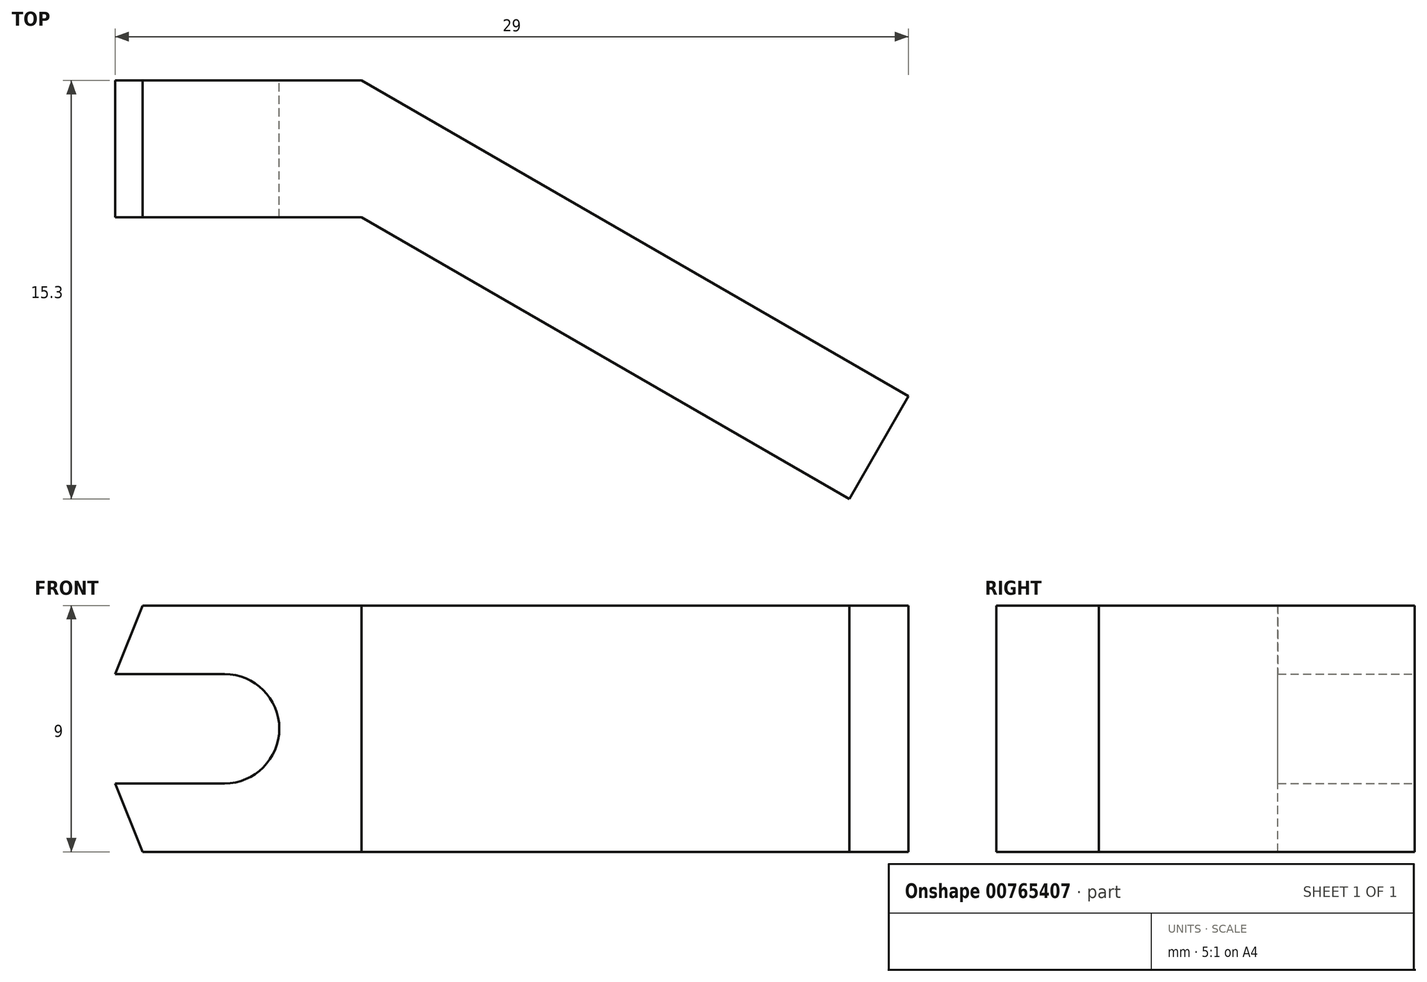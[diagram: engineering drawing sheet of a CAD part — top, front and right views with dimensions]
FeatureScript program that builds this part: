
annotation { "Feature Type Name" : "Feature", "Feature Type Description" : "" }
export const myFeature = defineFeature(function(context is Context, id is Id, definition is map)
    precondition{}
    {
        {
            var Q0;
            Q0=qCreatedBy(makeId("Front.planeOp"),FACE);
            var sketch = newSketch(context, id + "F0", { "sketchPlane" : qUnion([Q0])});
            skArc(sketch, "E0", {"start": v(0, -2) * mm, "mid": v(2, 0) * mm, "end": v(0, 2) * mm});
            skLineSegment(sketch, "E1", {"start": v(0, 2) * mm, "end": v(-4, 2) * mm});
            skLineSegment(sketch, "E2", {"start": v(0, -2) * mm, "end": v(-4, -2) * mm});
            skLineSegment(sketch, "E3", {"start": v(-3, -4.5) * mm, "end": v(-4, -2) * mm});
            skLineSegment(sketch, "E4", {"start": v(-3, 4.5) * mm, "end": v(-4, 2) * mm});
            skLineSegment(sketch, "E5", {"start": v(-3, -4.5) * mm, "end": v(5, -4.5) * mm});
            skLineSegment(sketch, "E6", {"start": v(5, -4.5) * mm, "end": v(5, 4.5) * mm});
            skLineSegment(sketch, "E7", {"start": v(5, 4.5) * mm, "end": v(-3, 4.5) * mm});
            skSolve(sketch);
        }
        {
            var Q0;
            Q0=makeQuery(id+"F0.imprint","IMPRINT",FACE,{"disambiguationData":[TD([[makeQuery(id+"F0.imprint","IMPRINT",EDGE,{"derivedFrom":sQuery(id+"F0.wireOp",EDGE,"E0")}),-1.0]])]});
            extrude(context, id + "F1", {"entities" : qUnion([Q0]), "depth" : 5 * mm, "offsetDistance" : 25 * mm});
        }
        {
            var Q0;
            Q0=makeQuery(id+"F1.opExtrude","SWEPT_FACE",FACE,{"disambiguationData":[OSD([sQuery(id+"F0.wireOp",EDGE,"E5")])]});
            var sketch = newSketch(context, id + "F2", { "sketchPlane" : qUnion([Q0])});
            skSolve(sketch);
        }
        {
            var Q0;
            {var subQ0=sQuery(id+"F0.wireOp",EDGE,"E5");Q0=makeQuery(id+"F2.imprint","IMPRINT",FACE,{"disambiguationData":[TD([[makeQuery(id+"F2.imprint","IMPRINT",EDGE,{"derivedFrom":makeQuery(id+"F1.opExtrude","CAP_EDGE",EDGE,{"disambiguationData":[OSD([subQ0])],"isStart":true})}),1.0]])]});}
            var sketch = newSketch(context, id + "F3", { "sketchPlane" : qUnion([Q0])});
            skLineSegment(sketch, "E8", {"start": v(5, 0) * mm, "end": v(25, 11.55) * mm});
            skLineSegment(sketch, "E9", {"start": v(22.83, 15.3) * mm, "end": v(5, 5) * mm});
            skLineSegment(sketch, "E10", {"start": v(25, 11.55) * mm, "end": v(22.83, 15.3) * mm});
            skSolve(sketch);
        }
        {
            var Q0;
            Q0=makeQuery(id+"F3.imprint","IMPRINT",FACE,{"disambiguationData":[TD([[makeQuery(id+"F3.imprint","IMPRINT",EDGE,{"derivedFrom":sQuery(id+"F3.wireOp",EDGE,"E8")}),1.0]])]});
            var Q1;
            Q1=makeQuery(id+"F1.opExtrude","SWEPT_FACE",FACE,{"disambiguationData":[OSD([sQuery(id+"F0.wireOp",EDGE,"E7")])]});
            extrude(context, id + "F4", {"entities" : qUnion([Q0]), "operationType" : NewBodyOperationType.ADD, "endBound" : BoundingType.UP_TO_SURFACE, "oppositeDirection" : true, "depth" : 25 * mm, "endBoundEntityFace" : qUnion([Q1]), "offsetDistance" : 25 * mm});
        }
    });
